# Revit family: EZTS+WITH 4 ROW HWC
name_source: partatom
category: Mechanical Equipment
revit_build: Autodesk Revit 2018 (Build: 20170223_1515(x64)
units: mm (PartAtom-declared; Revit-internal decimal feet)

## family parameters
Always vertical = Yes
Cut with Voids When Loaded = No
OmniClass Number = 23.75.00.00
OmniClass Title = Climate Control (HVAC)
Part Type = Normal
Room Calculation Point = No
Round Connector Dimension = Use Diameter
Shared = No
Work Plane-Based = No

## types (42) — shared parameters
Discharge = 0' - 0 5/8"
EnclosureFront = 0' - 3"
EnclosureHeight = 0' - 11 3/32"
EnclosureWidth = 0' - 7 1/8"
EnslosureRear = 1' - 2 7/32"
HWCOverlap = 0' - 0 5/8"
Inlet_S = 0' - 5 3/8"
PipeDia = 0' - 0 7/8"
PipeHTwo = 0' - 3 3/4"
PipeLength = 0' - 4"
PipeRad = 0' - 0 7/16"
PipeVOne = 0' - 1 1/4"
PipeVTwo = 0' - 1 1/4"
URL = https://www.anemostat-hvac.com

## per-type parameters (varying)
- EZTS+0508 W/4 Coil LH NO Controller: Coil=0' - 6 13/16"; Description=SINGLE DUCT AIR TERMINAL WITH JUMBO HOT WATER HEATING COIL; DischargeX=0' - 10 3/4"; DischargeY=0' - 8 3/4"; EnclosureCenter=0' - 5"; HWCSlipDrive=1' - 7 5/16"; HWCSlipDrive1Coil=1' - 3 5/8"; HWCSlipDrive2Coil=1' - 4 11/16"; HWCSlipDrive3Coil=1' - 5 3/4"; HWCSlipDrive4Coil=1' - 7 5/16"; Height=0' - 10"; InletDia=0' - 4 7/8"; InletRadius=0' - 2 7/16"; LeftController=No; Length=1' - 0 1/2"; Manufacturer=ANEMOSTAT PRODUCTS; Model=EZTS+; PipeHOne=0' - 3 15/16"; PipeOneLH=Yes; PipeOneRH=No; PipeTwoLH=Yes; PipeTwoRH=No; Power Left Controller=No; Power Right Controller=No; RightController=No; Width=1' - 0"
- EZTS+0608 W/4 Coil LH NO Controller: Coil=0' - 6 13/16"; Description=SINGLE DUCT AIR TERMINAL WITH JUMBO HOT WATER HEATING COIL; DischargeX=0' - 10 3/4"; DischargeY=0' - 8 3/4"; EnclosureCenter=0' - 5"; HWCSlipDrive=1' - 7 5/16"; HWCSlipDrive1Coil=1' - 3 5/8"; HWCSlipDrive2Coil=1' - 4 11/16"; HWCSlipDrive3Coil=1' - 5 3/4"; HWCSlipDrive4Coil=1' - 7 5/16"; Height=0' - 10"; InletDia=0' - 5 7/8"; InletRadius=0' - 2 15/16"; LeftController=No; Length=1' - 0 1/2"; Manufacturer=ANEMOSTAT PRODUCTS; Model=EZTS+; PipeHOne=0' - 3 15/16"; PipeOneLH=Yes; PipeOneRH=No; PipeTwoLH=Yes; PipeTwoRH=No; Power Left Controller=No; Power Right Controller=No; RightController=No; Width=1' - 0"
- EZTS+0508 W/4 Coil LH W/Controller LH: Coil=0' - 6 13/16"; Description=SINGLE DUCT AIR TERMINAL WITH JUMBO HOT WATER HEATING COIL; DischargeX=0' - 10 3/4"; DischargeY=0' - 8 3/4"; EnclosureCenter=0' - 5"; HWCSlipDrive=1' - 7 5/16"; HWCSlipDrive1Coil=1' - 3 5/8"; HWCSlipDrive2Coil=1' - 4 11/16"; HWCSlipDrive3Coil=1' - 5 3/4"; HWCSlipDrive4Coil=1' - 7 5/16"; Height=0' - 10"; InletDia=0' - 4 7/8"; InletRadius=0' - 2 7/16"; LeftController=Yes; Length=1' - 0 1/2"; Manufacturer=ANEMOSTAT PRODUCTS; Model=EZTS+; PipeHOne=0' - 3 15/16"; PipeOneLH=Yes; PipeOneRH=No; PipeTwoLH=Yes; PipeTwoRH=No; Power Left Controller=Yes; Power Right Controller=No; RightController=No; Width=1' - 0"
- EZTS+0608 W/4 Coil LH W/Controller LH: Coil=0' - 6 13/16"; Description=SINGLE DUCT AIR TERMINAL WITH JUMBO HOT WATER HEATING COIL; DischargeX=0' - 10 3/4"; DischargeY=0' - 8 3/4"; EnclosureCenter=0' - 5"; HWCSlipDrive=1' - 7 5/16"; HWCSlipDrive1Coil=1' - 3 5/8"; HWCSlipDrive2Coil=1' - 4 11/16"; HWCSlipDrive3Coil=1' - 5 3/4"; HWCSlipDrive4Coil=1' - 7 5/16"; Height=0' - 10"; InletDia=0' - 5 7/8"; InletRadius=0' - 2 15/16"; LeftController=Yes; Length=1' - 0 1/2"; Manufacturer=ANEMOSTAT PRODUCTS; Model=EZTS+; PipeHOne=0' - 3 15/16"; PipeOneLH=Yes; PipeOneRH=No; PipeTwoLH=Yes; PipeTwoRH=No; Power Left Controller=Yes; Power Right Controller=No; RightController=No; Width=1' - 0"
- EZTS+0508 W/4 Coil LH W/Controller RH: Coil=0' - 6 13/16"; Description=SINGLE DUCT AIR TERMINAL WITH JUMBO HOT WATER HEATING COIL; DischargeX=0' - 10 3/4"; DischargeY=0' - 8 3/4"; EnclosureCenter=0' - 5"; HWCSlipDrive=1' - 7 5/16"; HWCSlipDrive1Coil=1' - 3 5/8"; HWCSlipDrive2Coil=1' - 4 11/16"; HWCSlipDrive3Coil=1' - 5 3/4"; HWCSlipDrive4Coil=1' - 7 5/16"; Height=0' - 10"; InletDia=0' - 4 7/8"; InletRadius=0' - 2 7/16"; LeftController=No; Length=1' - 0 1/2"; Manufacturer=ANEMOSTAT PRODUCTS; Model=EZTS+; PipeHOne=0' - 3 15/16"; PipeOneLH=Yes; PipeOneRH=No; PipeTwoLH=Yes; PipeTwoRH=No; Power Left Controller=No; Power Right Controller=Yes; RightController=Yes; Width=1' - 0"
- EZTS+0608 W/4 Coil LH W/Controller RH: Coil=0' - 6 13/16"; Description=SINGLE DUCT AIR TERMINAL WITH JUMBO HOT WATER HEATING COIL; DischargeX=0' - 10 3/4"; DischargeY=0' - 8 3/4"; EnclosureCenter=0' - 5"; HWCSlipDrive=1' - 7 5/16"; HWCSlipDrive1Coil=1' - 3 5/8"; HWCSlipDrive2Coil=1' - 4 11/16"; HWCSlipDrive3Coil=1' - 5 3/4"; HWCSlipDrive4Coil=1' - 7 5/16"; Height=0' - 10"; InletDia=0' - 5 7/8"; InletRadius=0' - 2 15/16"; LeftController=No; Length=1' - 0 1/2"; Manufacturer=ANEMOSTAT PRODUCTS; Model=EZTS+; PipeHOne=0' - 3 15/16"; PipeOneLH=Yes; PipeOneRH=No; PipeTwoLH=Yes; PipeTwoRH=No; Power Left Controller=No; Power Right Controller=Yes; RightController=Yes; Width=1' - 0"
- EZTS+0508 W/4 Coil RH NO Controller: Coil=0' - 6 13/16"; Description=SINGLE DUCT AIR TERMINAL WITH JUMBO HOT WATER HEATING COIL; DischargeX=0' - 10 3/4"; DischargeY=0' - 8 3/4"; EnclosureCenter=0' - 5"; HWCSlipDrive=1' - 7 5/16"; HWCSlipDrive1Coil=1' - 3 5/8"; HWCSlipDrive2Coil=1' - 4 11/16"; HWCSlipDrive3Coil=1' - 5 3/4"; HWCSlipDrive4Coil=1' - 7 5/16"; Height=0' - 10"; InletDia=0' - 4 7/8"; InletRadius=0' - 2 7/16"; LeftController=No; Length=1' - 0 1/2"; Manufacturer=ANEMOSTAT PRODUCTS; Model=EZTS+; PipeHOne=0' - 3 15/16"; PipeOneLH=No; PipeOneRH=Yes; PipeTwoLH=No; PipeTwoRH=Yes; Power Left Controller=No; Power Right Controller=No; RightController=No; Width=1' - 0"
- EZTS+0608 W/4 Coil RH NO Controller: Coil=0' - 6 13/16"; Description=SINGLE DUCT AIR TERMINAL WITH JUMBO HOT WATER HEATING COIL; DischargeX=0' - 10 3/4"; DischargeY=0' - 8 3/4"; EnclosureCenter=0' - 5"; HWCSlipDrive=1' - 7 5/16"; HWCSlipDrive1Coil=1' - 3 5/8"; HWCSlipDrive2Coil=1' - 4 11/16"; HWCSlipDrive3Coil=1' - 5 3/4"; HWCSlipDrive4Coil=1' - 7 5/16"; Height=0' - 10"; InletDia=0' - 5 7/8"; InletRadius=0' - 2 15/16"; LeftController=No; Length=1' - 0 1/2"; Manufacturer=ANEMOSTAT PRODUCTS; Model=EZTS+; PipeHOne=0' - 3 15/16"; PipeOneLH=No; PipeOneRH=Yes; PipeTwoLH=No; PipeTwoRH=Yes; Power Left Controller=No; Power Right Controller=No; RightController=No; Width=1' - 0"
- EZTS+0508 W/4 Coil RH W/Controller LH: Coil=0' - 6 13/16"; Description=SINGLE DUCT AIR TERMINAL WITH JUMBO HOT WATER HEATING COIL; DischargeX=0' - 10 3/4"; DischargeY=0' - 8 3/4"; EnclosureCenter=0' - 5"; HWCSlipDrive=1' - 7 5/16"; HWCSlipDrive1Coil=1' - 3 5/8"; HWCSlipDrive2Coil=1' - 4 11/16"; HWCSlipDrive3Coil=1' - 5 3/4"; HWCSlipDrive4Coil=1' - 7 5/16"; Height=0' - 10"; InletDia=0' - 4 7/8"; InletRadius=0' - 2 7/16"; LeftController=Yes; Length=1' - 0 1/2"; Manufacturer=ANEMOSTAT PRODUCTS; Model=EZTS+; PipeHOne=0' - 3 15/16"; PipeOneLH=No; PipeOneRH=Yes; PipeTwoLH=No; PipeTwoRH=Yes; Power Left Controller=Yes; Power Right Controller=No; RightController=No; Width=1' - 0"
- EZTS+0608 W/4 Coil RH W/Controller LH: Coil=0' - 6 13/16"; Description=SINGLE DUCT AIR TERMINAL WITH JUMBO HOT WATER HEATING COIL; DischargeX=0' - 10 3/4"; DischargeY=0' - 8 3/4"; EnclosureCenter=0' - 5"; HWCSlipDrive=1' - 7 5/16"; HWCSlipDrive1Coil=1' - 3 5/8"; HWCSlipDrive2Coil=1' - 4 11/16"; HWCSlipDrive3Coil=1' - 5 3/4"; HWCSlipDrive4Coil=1' - 7 5/16"; Height=0' - 10"; InletDia=0' - 5 7/8"; InletRadius=0' - 2 15/16"; LeftController=Yes; Length=1' - 0 1/2"; Manufacturer=ANEMOSTAT PRODUCTS; Model=EZTS+; PipeHOne=0' - 3 15/16"; PipeOneLH=No; PipeOneRH=Yes; PipeTwoLH=No; PipeTwoRH=Yes; Power Left Controller=Yes; Power Right Controller=No; RightController=No; Width=1' - 0"
- EZTS+0508 W/4 Coil RH W/Controller RH: Coil=0' - 6 13/16"; Description=SINGLE DUCT AIR TERMINAL WITH JUMBO HOT WATER HEATING COIL; DischargeX=0' - 10 3/4"; DischargeY=0' - 8 3/4"; EnclosureCenter=0' - 5"; HWCSlipDrive=1' - 7 5/16"; HWCSlipDrive1Coil=1' - 3 5/8"; HWCSlipDrive2Coil=1' - 4 11/16"; HWCSlipDrive3Coil=1' - 5 3/4"; HWCSlipDrive4Coil=1' - 7 5/16"; Height=0' - 10"; InletDia=0' - 4 7/8"; InletRadius=0' - 2 7/16"; LeftController=No; Length=1' - 0 1/2"; Manufacturer=ANEMOSTAT PRODUCTS; Model=EZTS+; PipeHOne=0' - 3 15/16"; PipeOneLH=No; PipeOneRH=Yes; PipeTwoLH=No; PipeTwoRH=Yes; Power Left Controller=No; Power Right Controller=Yes; RightController=Yes; Width=1' - 0"
- EZTS+0608 W/4 Coil RH W/Controller RH: Coil=0' - 6 13/16"; Description=SINGLE DUCT AIR TERMINAL WITH JUMBO HOT WATER HEATING COIL; DischargeX=0' - 10 3/4"; DischargeY=0' - 8 3/4"; EnclosureCenter=0' - 5"; HWCSlipDrive=1' - 7 5/16"; HWCSlipDrive1Coil=1' - 3 5/8"; HWCSlipDrive2Coil=1' - 4 11/16"; HWCSlipDrive3Coil=1' - 5 3/4"; HWCSlipDrive4Coil=1' - 7 5/16"; Height=0' - 10"; InletDia=0' - 5 7/8"; InletRadius=0' - 2 15/16"; LeftController=No; Length=1' - 0 1/2"; Manufacturer=ANEMOSTAT PRODUCTS; Model=EZTS+; PipeHOne=0' - 3 15/16"; PipeOneLH=No; PipeOneRH=Yes; PipeTwoLH=No; PipeTwoRH=Yes; Power Left Controller=No; Power Right Controller=Yes; RightController=Yes; Width=1' - 0"
- EZTS+0710 W/4 Coil LH NO Controller: Coil=0' - 6 13/16"; Description=SINGLE DUCT AIR TERMINAL WITH JUMBO HOT WATER HEATING COIL; DischargeX=1' - 0 3/4"; DischargeY=0' - 11 1/4"; EnclosureCenter=0' - 6 1/4"; HWCSlipDrive=1' - 9 5/16"; HWCSlipDrive1Coil=1' - 5 5/8"; HWCSlipDrive2Coil=1' - 6 11/16"; HWCSlipDrive3Coil=1' - 7 3/4"; HWCSlipDrive4Coil=1' - 9 5/16"; Height=1' - 0 1/2"; InletDia=0' - 6 7/8"; InletRadius=0' - 3 7/16"; LeftController=No; Length=1' - 2 1/2"; Manufacturer=ANEMOSTAT PRODUCTS; Model=EZTS+; PipeHOne=0' - 3 15/16"; PipeOneLH=Yes; PipeOneRH=No; PipeTwoLH=Yes; PipeTwoRH=No; Power Left Controller=No; Power Right Controller=No; RightController=No; Width=1' - 2"
- EZTS+0810 W/4 Coil LH NO Controller: Coil=0' - 6 13/16"; Description=SINGLE DUCT AIR TERMINAL WITH JUMBO HOT WATER HEATING COIL; DischargeX=1' - 0 3/4"; DischargeY=0' - 11 1/4"; EnclosureCenter=0' - 6 1/4"; HWCSlipDrive=1' - 9 5/16"; HWCSlipDrive1Coil=1' - 5 5/8"; HWCSlipDrive2Coil=1' - 6 11/16"; HWCSlipDrive3Coil=1' - 7 3/4"; HWCSlipDrive4Coil=1' - 9 5/16"; Height=1' - 0 1/2"; InletDia=0' - 7 7/8"; InletRadius=0' - 3 15/16"; LeftController=No; Length=1' - 2 1/2"; Manufacturer=ANEMOSTAT PRODUCTS; Model=EZTS+; PipeHOne=0' - 3 15/16"; PipeOneLH=Yes; PipeOneRH=No; PipeTwoLH=Yes; PipeTwoRH=No; Power Left Controller=No; Power Right Controller=No; RightController=No; Width=1' - 2"
- EZTS+0710 W/4 Coil RH NO Controller: Coil=0' - 6 13/16"; Description=Single Duct Assembly with Hot Water Coil; DischargeX=1' - 0 3/4"; DischargeY=0' - 11 1/4"; EnclosureCenter=0' - 6 1/4"; HWCSlipDrive=1' - 9 5/16"; HWCSlipDrive1Coil=1' - 5 5/8"; HWCSlipDrive2Coil=1' - 6 11/16"; HWCSlipDrive3Coil=1' - 7 3/4"; HWCSlipDrive4Coil=1' - 9 5/16"; Height=1' - 0 1/2"; InletDia=0' - 6 7/8"; InletRadius=0' - 3 7/16"; LeftController=No; Length=1' - 2 1/2"; Manufacturer=ANEMOSTAT PRODUCTS; Model=EZTS+; PipeHOne=0' - 3 15/16"; PipeOneLH=No; PipeOneRH=Yes; PipeTwoLH=No; PipeTwoRH=Yes; Power Left Controller=No; Power Right Controller=No; RightController=No; Width=1' - 2"
- EZTS+0810 W/4 Coil RH NO Controller: Coil=0' - 6 13/16"; Description=Single Duct Assembly with Hot Water Coil; DischargeX=1' - 0 3/4"; DischargeY=0' - 11 1/4"; EnclosureCenter=0' - 6 1/4"; HWCSlipDrive=1' - 9 5/16"; HWCSlipDrive1Coil=1' - 5 5/8"; HWCSlipDrive2Coil=1' - 6 11/16"; HWCSlipDrive3Coil=1' - 7 3/4"; HWCSlipDrive4Coil=1' - 9 5/16"; Height=1' - 0 1/2"; InletDia=0' - 7 7/8"; InletRadius=0' - 3 15/16"; LeftController=No; Length=1' - 2 1/2"; Manufacturer=ANEMOSTAT PRODUCTS; Model=EZTS+; PipeHOne=0' - 3 15/16"; PipeOneLH=No; PipeOneRH=Yes; PipeTwoLH=No; PipeTwoRH=Yes; Power Left Controller=No; Power Right Controller=No; RightController=No; Width=1' - 2"
- EZTS+0710 W/4 Coil LH W/Controller LH: Coil=0' - 6 13/16"; Description=SINGLE DUCT AIR TERMINAL WITH JUMBO HOT WATER HEATING COIL; DischargeX=1' - 0 3/4"; DischargeY=0' - 11 1/4"; EnclosureCenter=0' - 6 1/4"; HWCSlipDrive=1' - 9 5/16"; HWCSlipDrive1Coil=1' - 5 5/8"; HWCSlipDrive2Coil=1' - 6 11/16"; HWCSlipDrive3Coil=1' - 7 3/4"; HWCSlipDrive4Coil=1' - 9 5/16"; Height=1' - 0 1/2"; InletDia=0' - 6 7/8"; InletRadius=0' - 3 7/16"; LeftController=Yes; Length=1' - 2 1/2"; Manufacturer=ANEMOSTAT PRODUCTS; Model=EZTS+; PipeHOne=0' - 3 15/16"; PipeOneLH=Yes; PipeOneRH=No; PipeTwoLH=Yes; PipeTwoRH=No; Power Left Controller=Yes; Power Right Controller=No; RightController=No; Width=1' - 2"
- EZTS+0810 W/4 Coil LH W/Controller LH: Coil=0' - 6 13/16"; Description=SINGLE DUCT AIR TERMINAL WITH JUMBO HOT WATER HEATING COIL; DischargeX=1' - 0 3/4"; DischargeY=0' - 11 1/4"; EnclosureCenter=0' - 6 1/4"; HWCSlipDrive=1' - 9 5/16"; HWCSlipDrive1Coil=1' - 5 5/8"; HWCSlipDrive2Coil=1' - 6 11/16"; HWCSlipDrive3Coil=1' - 7 3/4"; HWCSlipDrive4Coil=1' - 9 5/16"; Height=1' - 0 1/2"; InletDia=0' - 7 7/8"; InletRadius=0' - 3 15/16"; LeftController=Yes; Length=1' - 2 1/2"; Manufacturer=ANEMOSTAT PRODUCTS; Model=EZTS+; PipeHOne=0' - 3 15/16"; PipeOneLH=Yes; PipeOneRH=No; PipeTwoLH=Yes; PipeTwoRH=No; Power Left Controller=Yes; Power Right Controller=No; RightController=No; Width=1' - 2"
- EZTS+0710 W/4 Coil LH W/Controller RH: Coil=0' - 6 13/16"; Description=SINGLE DUCT AIR TERMINAL WITH JUMBO HOT WATER HEATING COIL; DischargeX=1' - 0 3/4"; DischargeY=0' - 11 1/4"; EnclosureCenter=0' - 6 1/4"; HWCSlipDrive=1' - 9 5/16"; HWCSlipDrive1Coil=1' - 5 5/8"; HWCSlipDrive2Coil=1' - 6 11/16"; HWCSlipDrive3Coil=1' - 7 3/4"; HWCSlipDrive4Coil=1' - 9 5/16"; Height=1' - 0 1/2"; InletDia=0' - 6 7/8"; InletRadius=0' - 3 7/16"; LeftController=No; Length=1' - 2 1/2"; Manufacturer=ANEMOSTAT PRODUCTS; Model=EZTS+; PipeHOne=0' - 3 15/16"; PipeOneLH=Yes; PipeOneRH=No; PipeTwoLH=Yes; PipeTwoRH=No; Power Left Controller=No; Power Right Controller=Yes; RightController=Yes; Width=1' - 2"
- EZTS+0810 W/4 Coil LH W/Controller RH: Coil=0' - 6 13/16"; Description=SINGLE DUCT AIR TERMINAL WITH JUMBO HOT WATER HEATING COIL; DischargeX=1' - 0 3/4"; DischargeY=0' - 11 1/4"; EnclosureCenter=0' - 6 1/4"; HWCSlipDrive=1' - 9 5/16"; HWCSlipDrive1Coil=1' - 5 5/8"; HWCSlipDrive2Coil=1' - 6 11/16"; HWCSlipDrive3Coil=1' - 7 3/4"; HWCSlipDrive4Coil=1' - 9 5/16"; Height=1' - 0 1/2"; InletDia=0' - 7 7/8"; InletRadius=0' - 3 15/16"; LeftController=No; Length=1' - 2 1/2"; Manufacturer=ANEMOSTAT PRODUCTS; Model=EZTS+; PipeHOne=0' - 3 15/16"; PipeOneLH=Yes; PipeOneRH=No; PipeTwoLH=Yes; PipeTwoRH=No; Power Left Controller=No; Power Right Controller=Yes; RightController=Yes; Width=1' - 2"
- EZTS+0710 W/4 Coil RH W/Controller LH: Coil=0' - 6 13/16"; Description=SINGLE DUCT AIR TERMINAL WITH JUMBO HOT WATER HEATING COIL; DischargeX=1' - 0 3/4"; DischargeY=0' - 11 1/4"; EnclosureCenter=0' - 6 1/4"; HWCSlipDrive=1' - 9 5/16"; HWCSlipDrive1Coil=1' - 5 5/8"; HWCSlipDrive2Coil=1' - 6 11/16"; HWCSlipDrive3Coil=1' - 7 3/4"; HWCSlipDrive4Coil=1' - 9 5/16"; Height=1' - 0 1/2"; InletDia=0' - 6 7/8"; InletRadius=0' - 3 7/16"; LeftController=Yes; Length=1' - 2 1/2"; Manufacturer=ANEMOSTAT PRODUCTS; Model=EZTS+; PipeHOne=0' - 3 15/16"; PipeOneLH=No; PipeOneRH=Yes; PipeTwoLH=No; PipeTwoRH=Yes; Power Left Controller=Yes; Power Right Controller=No; RightController=No; Width=1' - 2"
- EZTS+0810 W/4 Coil RH W/Controller LH: Coil=0' - 6 13/16"; Description=SINGLE DUCT AIR TERMINAL WITH JUMBO HOT WATER HEATING COIL; DischargeX=1' - 0 3/4"; DischargeY=0' - 11 1/4"; EnclosureCenter=0' - 6 1/4"; HWCSlipDrive=1' - 9 5/16"; HWCSlipDrive1Coil=1' - 5 5/8"; HWCSlipDrive2Coil=1' - 6 11/16"; HWCSlipDrive3Coil=1' - 7 3/4"; HWCSlipDrive4Coil=1' - 9 5/16"; Height=1' - 0 1/2"; InletDia=0' - 7 7/8"; InletRadius=0' - 3 15/16"; LeftController=Yes; Length=1' - 2 1/2"; Manufacturer=ANEMOSTAT PRODUCTS; Model=EZTS+; PipeHOne=0' - 3 15/16"; PipeOneLH=No; PipeOneRH=Yes; PipeTwoLH=No; PipeTwoRH=Yes; Power Left Controller=Yes; Power Right Controller=No; RightController=No; Width=1' - 2"
- EZTS+0710 W/4 Coil RH W/Controller RH: Coil=0' - 6 13/16"; Description=SINGLE DUCT AIR TERMINAL WITH JUMBO HOT WATER HEATING COIL; DischargeX=1' - 0 3/4"; DischargeY=0' - 11 1/4"; EnclosureCenter=0' - 6 1/4"; HWCSlipDrive=1' - 9 5/16"; HWCSlipDrive1Coil=1' - 5 5/8"; HWCSlipDrive2Coil=1' - 6 11/16"; HWCSlipDrive3Coil=1' - 7 3/4"; HWCSlipDrive4Coil=1' - 9 5/16"; Height=1' - 0 1/2"; InletDia=0' - 6 7/8"; InletRadius=0' - 3 7/16"; LeftController=No; Length=1' - 2 1/2"; Manufacturer=ANEMOSTAT PRODUCTS; Model=EZTS+; PipeHOne=0' - 3 15/16"; PipeOneLH=No; PipeOneRH=Yes; PipeTwoLH=No; PipeTwoRH=Yes; Power Left Controller=No; Power Right Controller=Yes; RightController=Yes; Width=1' - 2"
- EZTS+0810 W/4 Coil RH W/Controller RH: Coil=0' - 6 13/16"; Description=SINGLE DUCT AIR TERMINAL WITH JUMBO HOT WATER HEATING COIL; DischargeX=1' - 0 3/4"; DischargeY=0' - 11 1/4"; EnclosureCenter=0' - 6 1/4"; HWCSlipDrive=1' - 9 5/16"; HWCSlipDrive1Coil=1' - 5 5/8"; HWCSlipDrive2Coil=1' - 6 11/16"; HWCSlipDrive3Coil=1' - 7 3/4"; HWCSlipDrive4Coil=1' - 9 5/16"; Height=1' - 0 1/2"; InletDia=0' - 7 7/8"; InletRadius=0' - 3 15/16"; LeftController=No; Length=1' - 2 1/2"; Manufacturer=ANEMOSTAT PRODUCTS; Model=EZTS+; PipeHOne=0' - 3 15/16"; PipeOneLH=No; PipeOneRH=Yes; PipeTwoLH=No; PipeTwoRH=Yes; Power Left Controller=No; Power Right Controller=Yes; RightController=Yes; Width=1' - 2"
- EZTS+1012 W/4 Coil LH NO Controller: Coil=0' - 6 13/16"; Description=EZTS+ W/ Hot Water Heating Coil; DischargeX=1' - 2 3/4"; DischargeY=1' - 1 3/4"; EnclosureCenter=0' - 7 1/2"; HWCSlipDrive=2' - 1 5/16"; HWCSlipDrive1Coil=1' - 9 5/8"; HWCSlipDrive2Coil=1' - 10 11/16"; HWCSlipDrive3Coil=1' - 11 3/4"; HWCSlipDrive4Coil=2' - 1 5/16"; Height=1' - 3"; InletDia=0' - 9 7/8"; InletRadius=0' - 4 15/16"; LeftController=No; Length=1' - 6 1/2"; Manufacturer=ANEMOSTAT PRODUCTS; Model=EZTS+; PipeHOne=0' - 3 15/16"; PipeOneLH=Yes; PipeOneRH=No; PipeTwoLH=Yes; PipeTwoRH=No; Power Left Controller=No; Power Right Controller=No; RightController=No; Width=1' - 4"
- EZTS+1012 W/4 Coil RH NO Controller: Coil=0' - 6 13/16"; Description=EZTS+ W/ Hot Water Heating Coil; DischargeX=1' - 2 3/4"; DischargeY=1' - 1 3/4"; EnclosureCenter=0' - 7 1/2"; HWCSlipDrive=2' - 1 5/16"; HWCSlipDrive1Coil=1' - 9 5/8"; HWCSlipDrive2Coil=1' - 10 11/16"; HWCSlipDrive3Coil=1' - 11 3/4"; HWCSlipDrive4Coil=2' - 1 5/16"; Height=1' - 3"; InletDia=0' - 9 7/8"; InletRadius=0' - 4 15/16"; LeftController=No; Length=1' - 6 1/2"; Manufacturer=ANEMOSTAT PRODUCTS; Model=EZTS+; PipeHOne=0' - 3 15/16"; PipeOneLH=No; PipeOneRH=Yes; PipeTwoLH=No; PipeTwoRH=Yes; Power Left Controller=No; Power Right Controller=No; RightController=No; Width=1' - 4"
- EZTS+1012 W/4 Coil LH W/Controller LH: Coil=0' - 6 13/16"; Description=EZTS+ W/ Hot Water Heating Coil; DischargeX=1' - 2 3/4"; DischargeY=1' - 1 3/4"; EnclosureCenter=0' - 7 1/2"; HWCSlipDrive=2' - 1 5/16"; HWCSlipDrive1Coil=1' - 9 5/8"; HWCSlipDrive2Coil=1' - 10 11/16"; HWCSlipDrive3Coil=1' - 11 3/4"; HWCSlipDrive4Coil=2' - 1 5/16"; Height=1' - 3"; InletDia=0' - 9 7/8"; InletRadius=0' - 4 15/16"; LeftController=Yes; Length=1' - 6 1/2"; Manufacturer=ANEMOSTAT PRODUCTS; Model=EZTS+; PipeHOne=0' - 3 15/16"; PipeOneLH=Yes; PipeOneRH=No; PipeTwoLH=Yes; PipeTwoRH=No; Power Left Controller=Yes; Power Right Controller=No; RightController=No; Width=1' - 4"
- EZTS+1012 W/4 Coil LH W/Controller RH: Coil=0' - 6 13/16"; Description=EZTS+ W/ Hot Water Heating Coil; DischargeX=1' - 2 3/4"; DischargeY=1' - 1 3/4"; EnclosureCenter=0' - 7 1/2"; HWCSlipDrive=2' - 1 5/16"; HWCSlipDrive1Coil=1' - 9 5/8"; HWCSlipDrive2Coil=1' - 10 11/16"; HWCSlipDrive3Coil=1' - 11 3/4"; HWCSlipDrive4Coil=2' - 1 5/16"; Height=1' - 3"; InletDia=0' - 9 7/8"; InletRadius=0' - 4 15/16"; LeftController=No; Length=1' - 6 1/2"; Manufacturer=ANEMOSTAT PRODUCTS; Model=EZTS+; PipeHOne=0' - 3 15/16"; PipeOneLH=Yes; PipeOneRH=No; PipeTwoLH=Yes; PipeTwoRH=No; Power Left Controller=No; Power Right Controller=Yes; RightController=Yes; Width=1' - 4"
- EZTS+1012 W/4 Coil RH W/Controller LH: Coil=0' - 6 13/16"; Description=EZTS+ W/ Hot Water Heating Coil; DischargeX=1' - 2 3/4"; DischargeY=1' - 1 3/4"; EnclosureCenter=0' - 7 1/2"; HWCSlipDrive=2' - 1 5/16"; HWCSlipDrive1Coil=1' - 9 5/8"; HWCSlipDrive2Coil=1' - 10 11/16"; HWCSlipDrive3Coil=1' - 11 3/4"; HWCSlipDrive4Coil=2' - 1 5/16"; Height=1' - 3"; InletDia=0' - 9 7/8"; InletRadius=0' - 4 15/16"; LeftController=Yes; Length=1' - 6 1/2"; Manufacturer=ANEMOSTAT PRODUCTS; Model=EZTS+; PipeHOne=0' - 3 15/16"; PipeOneLH=No; PipeOneRH=Yes; PipeTwoLH=No; PipeTwoRH=Yes; Power Left Controller=Yes; Power Right Controller=No; RightController=No; Width=1' - 4"
- EZTS+1012 W/4 Coil RH W/Controller RH: Coil=0' - 6 13/16"; Description=EZTS+ W/ Hot Water Heating Coil; DischargeX=1' - 2 3/4"; DischargeY=1' - 1 3/4"; EnclosureCenter=0' - 7 1/2"; HWCSlipDrive=2' - 1 5/16"; HWCSlipDrive1Coil=1' - 9 5/8"; HWCSlipDrive2Coil=1' - 10 11/16"; HWCSlipDrive3Coil=1' - 11 3/4"; HWCSlipDrive4Coil=2' - 1 5/16"; Height=1' - 3"; InletDia=0' - 9 7/8"; InletRadius=0' - 4 15/16"; LeftController=No; Length=1' - 6 1/2"; Manufacturer=ANEMOSTAT PRODUCTS; Model=EZTS+; PipeHOne=0' - 3 15/16"; PipeOneLH=No; PipeOneRH=Yes; PipeTwoLH=No; PipeTwoRH=Yes; Power Left Controller=No; Power Right Controller=Yes; RightController=Yes; Width=1' - 4"
- EZTS+1214 W/4 Coil LH NO Controller: Coil=0' - 6 5/16"; Description=SINGLE DUCT AIR TERMINAL WITH JUMBO HOT WATER HEATING COIL; DischargeX=1' - 6 3/4"; DischargeY=1' - 4 1/4"; EnclosureCenter=0' - 8 3/4"; HWCSlipDrive=2' - 0 13/16"; HWCSlipDrive1Coil=1' - 9 5/8"; HWCSlipDrive2Coil=1' - 10 11/16"; HWCSlipDrive3Coil=1' - 11 3/4"; HWCSlipDrive4Coil=2' - 0 13/16"; Height=1' - 5 1/2"; InletDia=0' - 11 7/8"; InletRadius=0' - 5 15/16"; LeftController=No; Length=1' - 6 1/2"; Manufacturer=ANEMOSTAT PRODUCTS; Model=EZTS+; PipeHOne=0' - 3 23/32"; PipeOneLH=Yes; PipeOneRH=No; PipeTwoLH=Yes; PipeTwoRH=No; Power Left Controller=No; Power Right Controller=No; RightController=No; Width=1' - 8"
- EZTS+1214 W/4 Coil RH NO Controller: Coil=0' - 6 5/16"; Description=SINGLE DUCT AIR TERMINAL WITH JUMBO HOT WATER HEATING COIL; DischargeX=1' - 6 3/4"; DischargeY=1' - 4 1/4"; EnclosureCenter=0' - 8 3/4"; HWCSlipDrive=2' - 0 13/16"; HWCSlipDrive1Coil=1' - 9 5/8"; HWCSlipDrive2Coil=1' - 10 11/16"; HWCSlipDrive3Coil=1' - 11 3/4"; HWCSlipDrive4Coil=2' - 0 13/16"; Height=1' - 5 1/2"; InletDia=0' - 11 7/8"; InletRadius=0' - 5 15/16"; LeftController=No; Length=1' - 6 1/2"; Manufacturer=ANEMOSTAT PRODUCTS; Model=EZTS+; PipeHOne=0' - 3 23/32"; PipeOneLH=No; PipeOneRH=Yes; PipeTwoLH=No; PipeTwoRH=Yes; Power Left Controller=No; Power Right Controller=No; RightController=No; Width=1' - 8"
- EZTS+1214 W/4 Coil LH W/Controller LH: Coil=0' - 6 5/16"; Description=SINGLE DUCT AIR TERMINAL WITH JUMBO HOT WATER HEATING COIL; DischargeX=1' - 6 3/4"; DischargeY=1' - 4 1/4"; EnclosureCenter=0' - 8 3/4"; HWCSlipDrive=2' - 0 13/16"; HWCSlipDrive1Coil=1' - 9 5/8"; HWCSlipDrive2Coil=1' - 10 11/16"; HWCSlipDrive3Coil=1' - 11 3/4"; HWCSlipDrive4Coil=2' - 0 13/16"; Height=1' - 5 1/2"; InletDia=0' - 11 7/8"; InletRadius=0' - 5 15/16"; LeftController=Yes; Length=1' - 6 1/2"; Manufacturer=EZTS+; PipeHOne=0' - 3 23/32"; PipeOneLH=Yes; PipeOneRH=No; PipeTwoLH=Yes; PipeTwoRH=No; Power Left Controller=Yes; Power Right Controller=No; RightController=No; Type Comments=ANEMOSTAT PRODUCTS; Width=1' - 8"
- EZTS+1214 W/4 Coil LH W/Controller RH: Coil=0' - 6 5/16"; Description=SINGLE DUCT AIR TERMINAL WITH JUMBO HOT WATER HEATING COIL; DischargeX=1' - 6 3/4"; DischargeY=1' - 4 1/4"; EnclosureCenter=0' - 8 3/4"; HWCSlipDrive=2' - 0 13/16"; HWCSlipDrive1Coil=1' - 9 5/8"; HWCSlipDrive2Coil=1' - 10 11/16"; HWCSlipDrive3Coil=1' - 11 3/4"; HWCSlipDrive4Coil=2' - 0 13/16"; Height=1' - 5 1/2"; InletDia=0' - 11 7/8"; InletRadius=0' - 5 15/16"; LeftController=No; Length=1' - 6 1/2"; Manufacturer=ANEMOSTAT PRODUCTS; Model=EZTS+; PipeHOne=0' - 3 23/32"; PipeOneLH=Yes; PipeOneRH=No; PipeTwoLH=Yes; PipeTwoRH=No; Power Left Controller=No; Power Right Controller=Yes; RightController=Yes; Width=1' - 8"
- EZTS+1214 W/4 Coil RH W/Controller LH: Coil=0' - 6 5/16"; Description=SINGLE DUCT AIR TERMINAL WITH JUMBO HOT WATER HEATING COIL; DischargeX=1' - 6 3/4"; DischargeY=1' - 4 1/4"; EnclosureCenter=0' - 8 3/4"; HWCSlipDrive=2' - 0 13/16"; HWCSlipDrive1Coil=1' - 9 5/8"; HWCSlipDrive2Coil=1' - 10 11/16"; HWCSlipDrive3Coil=1' - 11 3/4"; HWCSlipDrive4Coil=2' - 0 13/16"; Height=1' - 5 1/2"; InletDia=0' - 11 7/8"; InletRadius=0' - 5 15/16"; LeftController=Yes; Length=1' - 6 1/2"; Manufacturer=ANEMOSTAT PRODUCTS; Model=EZTS+; PipeHOne=0' - 3 23/32"; PipeOneLH=No; PipeOneRH=Yes; PipeTwoLH=No; PipeTwoRH=Yes; Power Left Controller=Yes; Power Right Controller=No; RightController=No; Width=1' - 8"
- EZTS+1214 W/4 Coil RH W/Controller RH: Coil=0' - 6 5/16"; Description=SINGLE DUCT AIR TERMINAL WITH JUMBO HOT WATER HEATING COIL; DischargeX=1' - 6 3/4"; DischargeY=1' - 4 1/4"; EnclosureCenter=0' - 8 3/4"; HWCSlipDrive=2' - 0 13/16"; HWCSlipDrive1Coil=1' - 9 5/8"; HWCSlipDrive2Coil=1' - 10 11/16"; HWCSlipDrive3Coil=1' - 11 3/4"; HWCSlipDrive4Coil=2' - 0 13/16"; Height=1' - 5 1/2"; InletDia=0' - 11 7/8"; InletRadius=0' - 5 15/16"; LeftController=No; Length=1' - 6 1/2"; Manufacturer=ANEMOSTAT PRODUCTS; Model=EZTS+; PipeHOne=0' - 3 23/32"; PipeOneLH=No; PipeOneRH=Yes; PipeTwoLH=No; PipeTwoRH=Yes; Power Left Controller=No; Power Right Controller=Yes; RightController=Yes; Width=1' - 8"
- EZTS+1416 W/4 Coil LH NO Controller: Coil=0' - 6 5/16"; Description=SINGLE DUCT AIR TERMINAL WITH JUMBO HOT WATER HEATING COIL; DischargeX=1' - 10 3/4"; DischargeY=1' - 4 1/4"; EnclosureCenter=0' - 8 3/4"; HWCSlipDrive=2' - 0 13/16"; HWCSlipDrive1Coil=0' - 0"; HWCSlipDrive2Coil=1' - 10 11/16"; HWCSlipDrive3Coil=1' - 11 3/4"; HWCSlipDrive4Coil=2' - 0 13/16"; Height=1' - 5 1/2"; InletDia=1' - 1 7/8"; InletRadius=0' - 6 15/16"; LeftController=No; Length=1' - 6 1/2"; Manufacturer=ANEMOSTAT PRODUCTS; Model=EZTS+; PipeHOne=0' - 3 23/32"; PipeOneLH=Yes; PipeOneRH=No; PipeTwoLH=Yes; PipeTwoRH=No; Power Left Controller=No; Power Right Controller=No; RightController=No; Width=2' - 0"
- EZTS+1416 W/4 Coil RH NO Controller: Coil=0' - 6 5/16"; Description=SINGLE DUCT AIR TERMINAL WITH JUMBO HOT WATER HEATING COIL; DischargeX=1' - 10 3/4"; DischargeY=1' - 4 1/4"; EnclosureCenter=0' - 8 3/4"; HWCSlipDrive=2' - 0 13/16"; HWCSlipDrive1Coil=0' - 0"; HWCSlipDrive2Coil=1' - 10 11/16"; HWCSlipDrive3Coil=1' - 11 3/4"; HWCSlipDrive4Coil=2' - 0 13/16"; Height=1' - 5 1/2"; InletDia=1' - 1 7/8"; InletRadius=0' - 6 15/16"; LeftController=No; Length=1' - 6 1/2"; Manufacturer=ANEMOSTAT PRODUCTS; Model=EZTS+; PipeHOne=0' - 3 23/32"; PipeOneLH=No; PipeOneRH=Yes; PipeTwoLH=No; PipeTwoRH=Yes; Power Left Controller=No; Power Right Controller=No; RightController=No; Width=2' - 0"
- EZTS+1416 W/4 Coil LH W/Controller LH: Coil=0' - 6 5/16"; Description=SINGLE DUCT AIR TERMINAL WITH JUMBO HOT WATER HEATING COIL; DischargeX=1' - 10 3/4"; DischargeY=1' - 4 1/4"; EnclosureCenter=0' - 8 3/4"; HWCSlipDrive=2' - 0 13/16"; HWCSlipDrive1Coil=0' - 0"; HWCSlipDrive2Coil=1' - 10 11/16"; HWCSlipDrive3Coil=1' - 11 3/4"; HWCSlipDrive4Coil=2' - 0 13/16"; Height=1' - 5 1/2"; InletDia=1' - 1 7/8"; InletRadius=0' - 6 15/16"; LeftController=Yes; Length=1' - 6 1/2"; Manufacturer=ANEMOSTAT PRODUCTS; Model=EZTS+; PipeHOne=0' - 3 23/32"; PipeOneLH=Yes; PipeOneRH=No; PipeTwoLH=Yes; PipeTwoRH=No; Power Left Controller=Yes; Power Right Controller=No; RightController=No; Width=2' - 0"
- EZTS+1416 W/4 Coil LH W/Controller RH: Coil=0' - 6 5/16"; Description=SINGLE DUCT AIR TERMINAL WITH JUMBO HOT WATER HEATING COIL; DischargeX=1' - 10 3/4"; DischargeY=1' - 4 1/4"; EnclosureCenter=0' - 8 3/4"; HWCSlipDrive=2' - 0 13/16"; HWCSlipDrive1Coil=0' - 0"; HWCSlipDrive2Coil=1' - 10 11/16"; HWCSlipDrive3Coil=1' - 11 3/4"; HWCSlipDrive4Coil=2' - 0 13/16"; Height=1' - 5 1/2"; InletDia=1' - 1 7/8"; InletRadius=0' - 6 15/16"; LeftController=No; Length=1' - 6 1/2"; Manufacturer=ANEMOSTAT PRODUCTS; Model=EZTS+; PipeHOne=0' - 3 23/32"; PipeOneLH=Yes; PipeOneRH=No; PipeTwoLH=Yes; PipeTwoRH=No; Power Left Controller=No; Power Right Controller=Yes; RightController=Yes; Width=2' - 0"
- EZTS+1416 W/4 Coil RH W/Controller LH: Coil=0' - 6 5/16"; Description=SINGLE DUCT AIR TERMINAL WITH JUMBO HOT WATER HEATING COIL; DischargeX=1' - 10 3/4"; DischargeY=1' - 4 1/4"; EnclosureCenter=0' - 8 3/4"; HWCSlipDrive=2' - 0 13/16"; HWCSlipDrive1Coil=0' - 0"; HWCSlipDrive2Coil=1' - 10 11/16"; HWCSlipDrive3Coil=1' - 11 3/4"; HWCSlipDrive4Coil=2' - 0 13/16"; Height=1' - 5 1/2"; InletDia=1' - 1 7/8"; InletRadius=0' - 6 15/16"; LeftController=Yes; Length=1' - 6 1/2"; Manufacturer=ANEMOSTAT PRODUCTS; Model=EZTS+; PipeHOne=0' - 3 23/32"; PipeOneLH=No; PipeOneRH=Yes; PipeTwoLH=No; PipeTwoRH=Yes; Power Left Controller=Yes; Power Right Controller=No; RightController=No; Width=2' - 0"
- EZTS+1416 W/4 Coil RH W/Controller RH: Coil=0' - 6 5/16"; Description=EZTS+ W/ Hot Water Heating Coil; DischargeX=1' - 10 3/4"; DischargeY=1' - 4 1/4"; EnclosureCenter=0' - 8 3/4"; HWCSlipDrive=2' - 0 13/16"; HWCSlipDrive1Coil=0' - 0"; HWCSlipDrive2Coil=1' - 10 11/16"; HWCSlipDrive3Coil=1' - 11 3/4"; HWCSlipDrive4Coil=2' - 0 13/16"; Height=1' - 5 1/2"; InletDia=1' - 1 7/8"; InletRadius=0' - 6 15/16"; LeftController=No; Length=1' - 6 1/2"; Manufacturer=ANEMOSTAT PRODUCTS; Model=EZTS+; PipeHOne=0' - 3 23/32"; PipeOneLH=No; PipeOneRH=Yes; PipeTwoLH=No; PipeTwoRH=Yes; Power Left Controller=No; Power Right Controller=Yes; RightController=Yes; Width=2' - 0"

## geometry (parser evidence)
native form markers: Sweep x3
no freeform markers — native parametric forms only
